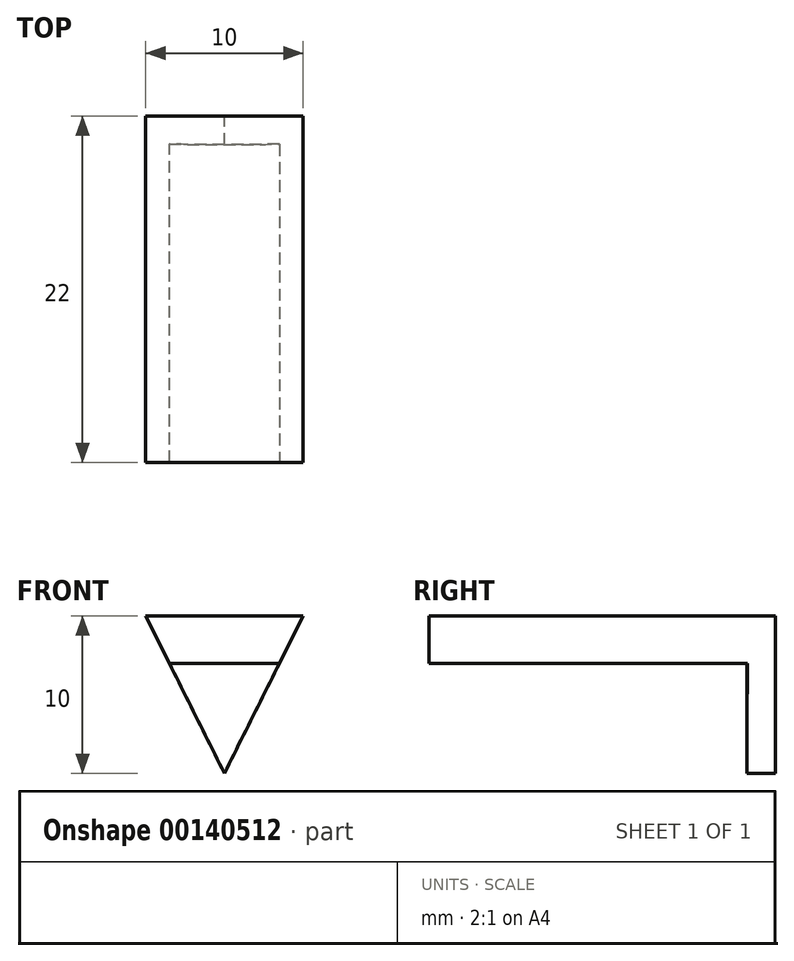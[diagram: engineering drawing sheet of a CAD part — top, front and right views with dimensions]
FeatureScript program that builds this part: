
annotation { "Feature Type Name" : "Feature", "Feature Type Description" : "" }
export const myFeature = defineFeature(function(context is Context, id is Id, definition is map)
    precondition{}
    {
        {
            var Q0;
            Q0=qCreatedBy(makeId("Front.planeOp"),FACE);
            var sketch = newSketch(context, id + "F0", { "sketchPlane" : qUnion([Q0])});
            skLineSegment(sketch, "E0", {"start": v(0, 0) * mm, "end": v(5, 0) * mm});
            skLineSegment(sketch, "E1", {"start": v(5, -10) * mm, "end": v(0, 0) * mm});
            skLineSegment(sketch, "E2", {"start": v(5, 0) * mm, "end": v(10, 0) * mm});
            skLineSegment(sketch, "E3", {"start": v(10, 0) * mm, "end": v(5, -10) * mm});
            skLineSegment(sketch, "E4", {"start": v(1.5, -3) * mm, "end": v(8.5, -3) * mm});
            skSolve(sketch);
        }
        {
            var Q0;
            Q0=qCreatedBy(makeId("Top.planeOp"),FACE);
            var sketch = newSketch(context, id + "F1", { "sketchPlane" : qUnion([Q0])});
            skLineSegment(sketch, "E5", {"start": v(0, 0) * mm, "end": v(0, -4.98) * mm});
            skLineSegment(sketch, "E6", {"start": v(0, 0) * mm, "end": v(10, 0) * mm});
            skLineSegment(sketch, "E7", {"start": v(10, 0) * mm, "end": v(10, -4.98) * mm});
            skLineSegment(sketch, "E8", {"start": v(0, 0) * mm, "end": v(0, 137) * mm});
            skLineSegment(sketch, "E9", {"start": v(0, 137) * mm, "end": v(5, 137) * mm});
            skArc(sketch, "E10", {"start": v(0, -4.98) * mm, "mid": v(5, -5.07) * mm, "end": v(10, -4.98) * mm});
            skLineSegment(sketch, "E11", {"start": v(0, -4.98) * mm, "end": v(0, -23) * mm});
            skLineSegment(sketch, "E12", {"start": v(0, -23) * mm, "end": v(10, -23) * mm});
            skLineSegment(sketch, "E13", {"start": v(10, -23) * mm, "end": v(10, -4.98) * mm});
            skCircle(sketch, "E14", {"center": v(5, 137) * mm, "radius": 138.82 * mm});
            skSolve(sketch);
        }
        {
            var Q0;
            {var subQ4=sQuery(id+"F0.wireOp",EDGE,"E0");Q0=makeQuery(id+"F0.imprint","IMPRINT",FACE,{"disambiguationData":[TD([[makeQuery(id+"F0.imprint","IMPRINT",EDGE,{"derivedFrom":subQ4}),-1.0]])]});}
            var Q1;
            {var subQ3=sQuery(id+"F0.wireOp",EDGE,"E4");Q1=makeQuery(id+"F0.imprint","IMPRINT",FACE,{"disambiguationData":[TD([[makeQuery(id+"F0.imprint","IMPRINT",EDGE,{"derivedFrom":subQ3}),-1.0]])]});}
            extrude(context, id + "F2", {"entities" : qUnion([Q0, Q1]), "depth" : 22 * mm});
        }
        {
            var Q0;
            {var subQ0=sQuery(id+"F1.wireOp",EDGE,"E10");Q0=makeQuery(id+"F1.imprint","IMPRINT",FACE,{"disambiguationData":[TD([[makeQuery(id+"F1.imprint","IMPRINT",EDGE,{"derivedFrom":subQ0}),1.0]])]});}
            var Q1;
            Q1=makeQuery(id+"F1.imprint","IMPRINT",FACE,{"disambiguationData":[TD([[makeQuery(id+"F1.imprint","IMPRINT",EDGE,{"derivedFrom":sQuery(id+"F1.wireOp",EDGE,"E10")}),-1.0]])]});
            extrude(context, id + "F3", {"entities" : qUnion([Q0, Q1]), "operationType" : NewBodyOperationType.REMOVE, "oppositeDirection" : true, "depth" : 10 * mm, "hasSecondDirection" : true, "secondDirectionOppositeDirection" : true, "secondDirectionDepth" : 3 * mm});
        }
    });
